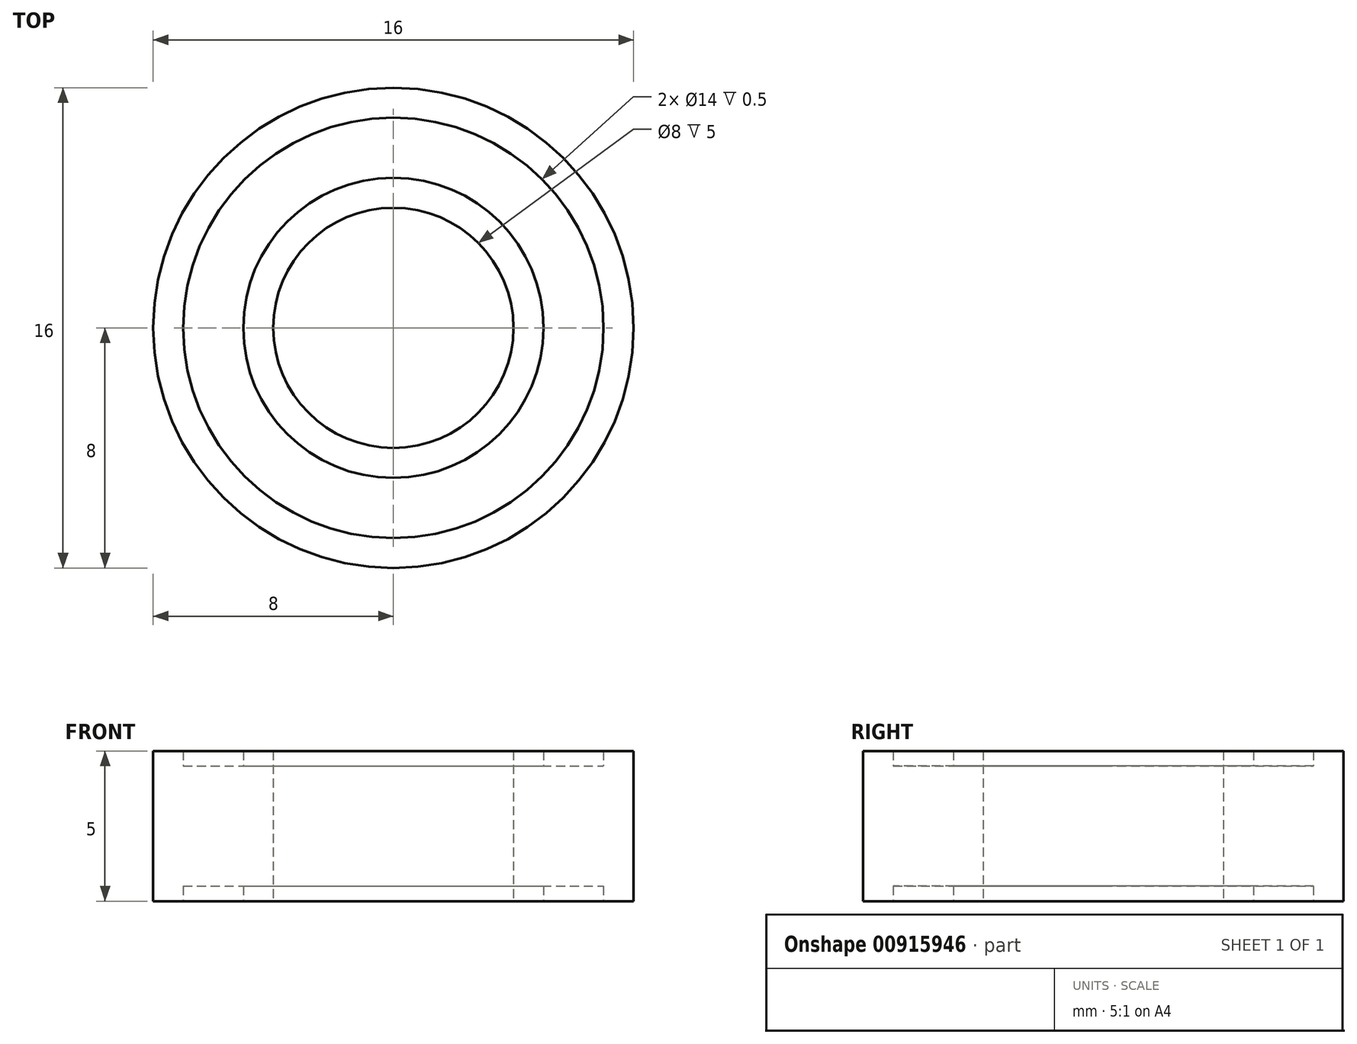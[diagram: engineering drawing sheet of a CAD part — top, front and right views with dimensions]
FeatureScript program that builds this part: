
annotation { "Feature Type Name" : "Feature", "Feature Type Description" : "" }
export const myFeature = defineFeature(function(context is Context, id is Id, definition is map)
    precondition{}
    {
        {
            var Q0;
            Q0=qCreatedBy(makeId("Right.planeOp"),FACE);
            var sketch = newSketch(context, id + "F0", { "sketchPlane" : qUnion([Q0])});
            skLineSegment(sketch, "E0", {"start": v(0, 0) * mm, "end": v(0, 5) * mm});
            skLineSegment(sketch, "E1", {"start": v(4, 0) * mm, "end": v(4, 5) * mm});
            skLineSegment(sketch, "E2", {"start": v(4, 5) * mm, "end": v(5, 5) * mm});
            skLineSegment(sketch, "E3", {"start": v(5, 5) * mm, "end": v(5, 4.5) * mm});
            skLineSegment(sketch, "E4", {"start": v(5, 4.5) * mm, "end": v(7, 4.5) * mm});
            skLineSegment(sketch, "E5", {"start": v(7, 4.5) * mm, "end": v(7, 5) * mm});
            skLineSegment(sketch, "E6", {"start": v(7, 5) * mm, "end": v(8, 5) * mm});
            skLineSegment(sketch, "E7", {"start": v(8, 5) * mm, "end": v(8, 0) * mm});
            skLineSegment(sketch, "E8", {"start": v(8, 0) * mm, "end": v(7, 0) * mm});
            skLineSegment(sketch, "E9", {"start": v(7, 0) * mm, "end": v(7, 0.5) * mm});
            skLineSegment(sketch, "E10", {"start": v(7, 0.5) * mm, "end": v(5, 0.5) * mm});
            skLineSegment(sketch, "E11", {"start": v(5, 0.5) * mm, "end": v(5, 0) * mm});
            skLineSegment(sketch, "E12", {"start": v(5, 0) * mm, "end": v(4, 0) * mm});
            skSolve(sketch);
        }
        {
            var Q0;
            Q0=makeQuery(id+"F0.imprint","IMPRINT",FACE,{"disambiguationData":[TD([[makeQuery(id+"F0.imprint","IMPRINT",EDGE,{"derivedFrom":sQuery(id+"F0.wireOp",EDGE,"E1")}),-1.0]])]});
            var Q1;
            Q1=sQuery(id+"F0.wireOp",EDGE,"E0");
            revolve(context, id + "F1", {"surfaceOperationType" : NewSurfaceOperationType.NEW, "entities" : qUnion([Q0]), "axis" : qUnion([Q1]), "revolveType" : RevolveType.FULL});
        }
    });
